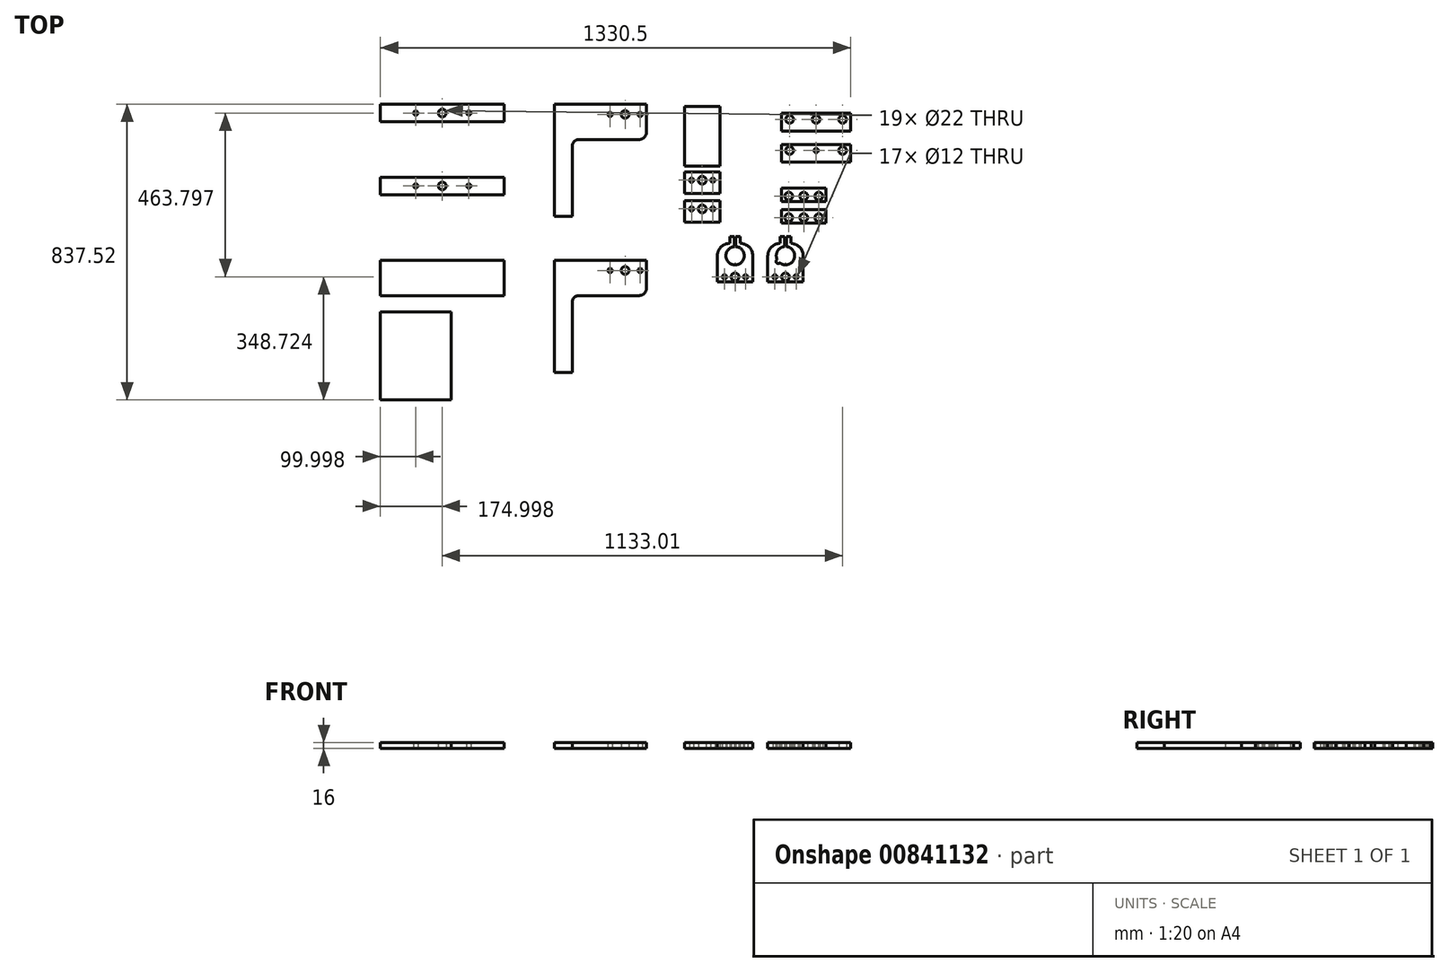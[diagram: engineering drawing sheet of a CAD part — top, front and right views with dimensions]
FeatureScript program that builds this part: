
annotation { "Feature Type Name" : "Feature", "Feature Type Description" : "" }
export const myFeature = defineFeature(function(context is Context, id is Id, definition is map)
    precondition{}
    {
        {
            var Q0;
            Q0=qCreatedBy(makeId("Top.planeOp"),FACE);
            var sketch = newSketch(context, id + "F0", { "sketchPlane" : qUnion([Q0])});
            skLineSegment(sketch, "E0.bottom", {"start": v(-793.1, 335.3) * mm, "end": v(-443.1, 335.3) * mm});
            skLineSegment(sketch, "E0.top", {"start": v(-793.1, 285.3) * mm, "end": v(-443.1, 285.3) * mm});
            skLineSegment(sketch, "E0.left", {"start": v(-793.1, 335.3) * mm, "end": v(-793.1, 285.3) * mm});
            skLineSegment(sketch, "E0.right", {"start": v(-443.1, 335.3) * mm, "end": v(-443.1, 285.3) * mm});
            skLineSegment(sketch, "E1.bottom", {"start": v(-793.1, 100) * mm, "end": v(-443.1, 100) * mm});
            skLineSegment(sketch, "E1.top", {"start": v(-793.1, 0) * mm, "end": v(-443.1, 0) * mm});
            skLineSegment(sketch, "E1.left", {"start": v(-793.1, 100) * mm, "end": v(-793.1, 0) * mm});
            skLineSegment(sketch, "E1.right", {"start": v(-443.1, 100) * mm, "end": v(-443.1, 0) * mm});
            skLineSegment(sketch, "E2", {"start": v(-300.58, 541.75) * mm, "end": v(-40.58, 541.75) * mm});
            skLineSegment(sketch, "E3", {"start": v(-40.58, 541.75) * mm, "end": v(-40.58, 461.75) * mm});
            skLineSegment(sketch, "E4", {"start": v(-60.58, 441.75) * mm, "end": v(-230.58, 441.75) * mm});
            skLineSegment(sketch, "E5", {"start": v(-250.58, 421.75) * mm, "end": v(-250.58, 223.75) * mm});
            skLineSegment(sketch, "E6", {"start": v(-250.58, 223.75) * mm, "end": v(-300.58, 223.75) * mm});
            skLineSegment(sketch, "E7", {"start": v(-300.58, 223.75) * mm, "end": v(-300.58, 541.75) * mm});
            skCircle(sketch, "E8", {"center": v(-693.1, 310.3) * mm, "radius": 6 * mm});
            skCircle(sketch, "E9", {"center": v(-543.1, 310.3) * mm, "radius": 6 * mm});
            skLineSegment(sketch, "E10", {"start": v(-793.1, 310.3) * mm, "end": v(-443.1, 310.3) * mm, "construction": true});
            skCircle(sketch, "E11", {"center": v(-618.1, 310.3) * mm, "radius": 11 * mm});
            skLineSegment(sketch, "E12.bottom", {"start": v(-793.1, 541.75) * mm, "end": v(-443.1, 541.75) * mm});
            skLineSegment(sketch, "E12.top", {"start": v(-793.1, 491.75) * mm, "end": v(-443.1, 491.75) * mm});
            skLineSegment(sketch, "E12.left", {"start": v(-793.1, 541.75) * mm, "end": v(-793.1, 491.75) * mm});
            skLineSegment(sketch, "E12.right", {"start": v(-443.1, 541.75) * mm, "end": v(-443.1, 491.75) * mm});
            skLineSegment(sketch, "E13", {"start": v(-793.1, 516.75) * mm, "end": v(-443.1, 516.75) * mm, "construction": true});
            skCircle(sketch, "E14", {"center": v(-693.1, 516.75) * mm, "radius": 6 * mm});
            skCircle(sketch, "E15", {"center": v(-543.1, 516.75) * mm, "radius": 6 * mm});
            skCircle(sketch, "E16", {"center": v(-618.1, 516.75) * mm, "radius": 11 * mm});
            skLineSegment(sketch, "E17", {"start": v(-300.58, 100) * mm, "end": v(-40.58, 100) * mm});
            skLineSegment(sketch, "E18", {"start": v(-40.58, 100) * mm, "end": v(-40.58, 20) * mm});
            skLineSegment(sketch, "E19", {"start": v(-60.58, 0) * mm, "end": v(-230.58, 0) * mm});
            skLineSegment(sketch, "E20", {"start": v(-250.58, -20) * mm, "end": v(-250.58, -218) * mm});
            skLineSegment(sketch, "E21", {"start": v(-250.58, -218) * mm, "end": v(-300.58, -218) * mm});
            skLineSegment(sketch, "E22", {"start": v(-300.58, -218) * mm, "end": v(-300.58, 100) * mm});
            skLineSegment(sketch, "E23", {"start": v(-40.58, 512.75) * mm, "end": v(-300.58, 512.75) * mm, "construction": true});
            skLineSegment(sketch, "E24", {"start": v(-40.58, 71) * mm, "end": v(-300.58, 71) * mm, "construction": true});
            skCircle(sketch, "E25", {"center": v(-58.15, 512.75) * mm, "radius": 6 * mm});
            skCircle(sketch, "E26", {"center": v(-143.15, 512.75) * mm, "radius": 6 * mm});
            skCircle(sketch, "E27", {"center": v(-58.15, 71) * mm, "radius": 6 * mm});
            skCircle(sketch, "E28", {"center": v(-143.15, 71) * mm, "radius": 6 * mm});
            skCircle(sketch, "E29", {"center": v(-100.58, 512.75) * mm, "radius": 11 * mm});
            skCircle(sketch, "E30", {"center": v(-100.58, 71) * mm, "radius": 11 * mm});
            skPoint(sketch, "E31.visualSharp", {"position": v(-40.58, 441.75) * mm});
            skArc(sketch, "E31.filletArc", {"start": v(-60.58, 441.75) * mm, "mid": v(-46.44, 447.6) * mm, "end": v(-40.58, 461.75) * mm});
            skPoint(sketch, "E32.visualSharp", {"position": v(-250.58, 441.75) * mm});
            skArc(sketch, "E32.filletArc", {"start": v(-230.58, 441.75) * mm, "mid": v(-244.73, 435.9) * mm, "end": v(-250.58, 421.75) * mm});
            skPoint(sketch, "E33.visualSharp", {"position": v(-40.58, 0) * mm});
            skArc(sketch, "E33.filletArc", {"start": v(-60.58, 0) * mm, "mid": v(-46.44, 5.86) * mm, "end": v(-40.58, 20) * mm});
            skPoint(sketch, "E34.visualSharp", {"position": v(-250.58, 0) * mm});
            skArc(sketch, "E34.filletArc", {"start": v(-230.58, 0) * mm, "mid": v(-244.73, -5.86) * mm, "end": v(-250.58, -20) * mm});
            skLineSegment(sketch, "E35.bottom", {"start": v(-793.1, -45.77) * mm, "end": v(-593.1, -45.77) * mm});
            skLineSegment(sketch, "E35.top", {"start": v(-793.1, -295.77) * mm, "end": v(-593.1, -295.77) * mm});
            skLineSegment(sketch, "E35.left", {"start": v(-793.1, -45.77) * mm, "end": v(-793.1, -295.77) * mm});
            skLineSegment(sketch, "E35.right", {"start": v(-593.1, -45.77) * mm, "end": v(-593.1, -295.77) * mm});
            skLineSegment(sketch, "E36.bottom", {"start": v(67.56, 535) * mm, "end": v(167.56, 535) * mm});
            skLineSegment(sketch, "E36.top", {"start": v(67.56, 367) * mm, "end": v(167.56, 367) * mm});
            skLineSegment(sketch, "E36.left", {"start": v(67.56, 535) * mm, "end": v(67.56, 367) * mm});
            skLineSegment(sketch, "E36.right", {"start": v(167.56, 535) * mm, "end": v(167.56, 367) * mm});
            skLineSegment(sketch, "E37.bottom", {"start": v(67.56, 349.5) * mm, "end": v(167.56, 349.5) * mm});
            skLineSegment(sketch, "E37.top", {"start": v(67.56, 289.5) * mm, "end": v(167.56, 289.5) * mm});
            skLineSegment(sketch, "E37.left", {"start": v(67.56, 349.5) * mm, "end": v(67.56, 289.5) * mm});
            skLineSegment(sketch, "E37.right", {"start": v(167.56, 349.5) * mm, "end": v(167.56, 289.5) * mm});
            skPoint(sketch, "E38.oppositeSnap0", {"position": v(167.56, 319.5) * mm});
            skLineSegment(sketch, "E39.bottom", {"start": v(342.4, 515.9) * mm, "end": v(537.4, 515.9) * mm});
            skLineSegment(sketch, "E39.top", {"start": v(342.4, 465.9) * mm, "end": v(537.4, 465.9) * mm});
            skLineSegment(sketch, "E39.left", {"start": v(342.4, 515.9) * mm, "end": v(342.4, 465.9) * mm});
            skLineSegment(sketch, "E39.right", {"start": v(537.4, 515.9) * mm, "end": v(537.4, 465.9) * mm});
            skLineSegment(sketch, "E40", {"start": v(67.56, 326.5) * mm, "end": v(167.56, 326.5) * mm, "construction": true});
            skCircle(sketch, "E41", {"center": v(117.56, 326.5) * mm, "radius": 11 * mm});
            skCircle(sketch, "E42", {"center": v(87.56, 326.5) * mm, "radius": 6 * mm});
            skCircle(sketch, "E43", {"center": v(147.56, 326.5) * mm, "radius": 6 * mm});
            skLineSegment(sketch, "E44.bottom", {"start": v(67.56, 268.28) * mm, "end": v(167.56, 268.28) * mm});
            skLineSegment(sketch, "E44.top", {"start": v(67.56, 208.28) * mm, "end": v(167.56, 208.28) * mm});
            skLineSegment(sketch, "E44.left", {"start": v(67.56, 268.28) * mm, "end": v(67.56, 208.28) * mm});
            skLineSegment(sketch, "E44.right", {"start": v(167.56, 268.28) * mm, "end": v(167.56, 208.28) * mm});
            skPoint(sketch, "E45.oppositeSnap0", {"position": v(167.56, 238.28) * mm});
            skLineSegment(sketch, "E46", {"start": v(67.56, 245.28) * mm, "end": v(167.56, 245.28) * mm, "construction": true});
            skCircle(sketch, "E47", {"center": v(117.56, 245.28) * mm, "radius": 11 * mm});
            skCircle(sketch, "E48", {"center": v(87.56, 245.28) * mm, "radius": 6 * mm});
            skCircle(sketch, "E49", {"center": v(147.56, 245.28) * mm, "radius": 6 * mm});
            skLineSegment(sketch, "E50", {"start": v(342.4, 498.9) * mm, "end": v(537.4, 498.9) * mm, "construction": true});
            skCircle(sketch, "E51", {"center": v(364.9, 498.9) * mm, "radius": 11 * mm});
            skCircle(sketch, "E52", {"center": v(514.9, 498.9) * mm, "radius": 11 * mm});
            skCircle(sketch, "E53", {"center": v(439.9, 498.9) * mm, "radius": 11 * mm});
            skLineSegment(sketch, "E54.bottom", {"start": v(342.4, 427.64) * mm, "end": v(537.4, 427.64) * mm});
            skLineSegment(sketch, "E54.top", {"start": v(342.4, 377.64) * mm, "end": v(537.4, 377.64) * mm});
            skLineSegment(sketch, "E54.left", {"start": v(342.4, 427.64) * mm, "end": v(342.4, 377.64) * mm});
            skLineSegment(sketch, "E54.right", {"start": v(537.4, 427.64) * mm, "end": v(537.4, 377.64) * mm});
            skLineSegment(sketch, "E55", {"start": v(342.4, 410.64) * mm, "end": v(537.4, 410.64) * mm, "construction": true});
            skCircle(sketch, "E56", {"center": v(364.9, 410.64) * mm, "radius": 11 * mm});
            skCircle(sketch, "E57", {"center": v(514.9, 410.64) * mm, "radius": 11 * mm});
            skCircle(sketch, "E58", {"center": v(439.9, 410.64) * mm, "radius": 6 * mm});
            skLineSegment(sketch, "E59.bottom", {"start": v(342.4, 304.54) * mm, "end": v(467.4, 304.54) * mm});
            skLineSegment(sketch, "E59.top", {"start": v(342.4, 266.54) * mm, "end": v(467.4, 266.54) * mm});
            skLineSegment(sketch, "E59.left", {"start": v(342.4, 304.54) * mm, "end": v(342.4, 266.54) * mm});
            skLineSegment(sketch, "E59.right", {"start": v(467.4, 304.54) * mm, "end": v(467.4, 266.54) * mm});
            skPoint(sketch, "E60.oppositeSnap0", {"position": v(467.4, 285.54) * mm});
            skLineSegment(sketch, "E61", {"start": v(342.4, 281.54) * mm, "end": v(467.4, 281.54) * mm, "construction": true});
            skCircle(sketch, "E62", {"center": v(404.9, 281.54) * mm, "radius": 11 * mm});
            skCircle(sketch, "E63", {"center": v(362.4, 281.54) * mm, "radius": 11 * mm});
            skCircle(sketch, "E64", {"center": v(447.4, 281.54) * mm, "radius": 11 * mm});
            skLineSegment(sketch, "E65.bottom", {"start": v(342.4, 243.72) * mm, "end": v(467.4, 243.72) * mm});
            skLineSegment(sketch, "E65.top", {"start": v(342.4, 205.72) * mm, "end": v(467.4, 205.72) * mm});
            skLineSegment(sketch, "E65.left", {"start": v(342.4, 243.72) * mm, "end": v(342.4, 205.72) * mm});
            skLineSegment(sketch, "E65.right", {"start": v(467.4, 243.72) * mm, "end": v(467.4, 205.72) * mm});
            skPoint(sketch, "E66.oppositeSnap0", {"position": v(467.4, 224.72) * mm});
            skLineSegment(sketch, "E67", {"start": v(342.4, 220.72) * mm, "end": v(467.4, 220.72) * mm, "construction": true});
            skCircle(sketch, "E68", {"center": v(404.9, 220.72) * mm, "radius": 11 * mm});
            skCircle(sketch, "E69", {"center": v(362.4, 220.72) * mm, "radius": 11 * mm});
            skCircle(sketch, "E70", {"center": v(447.4, 220.72) * mm, "radius": 11 * mm});
            skLineSegment(sketch, "E71.bottom", {"start": v(160.46, 78.95) * mm, "end": v(260.46, 78.95) * mm});
            skLineSegment(sketch, "E71.top", {"start": v(160.46, 38.95) * mm, "end": v(260.46, 38.95) * mm});
            skLineSegment(sketch, "E71.left", {"start": v(160.46, 78.95) * mm, "end": v(160.46, 38.95) * mm});
            skLineSegment(sketch, "E71.right", {"start": v(260.46, 78.95) * mm, "end": v(260.46, 38.95) * mm});
            skPoint(sketch, "E72.oppositeSnap0", {"position": v(260.46, 58.95) * mm});
            skLineSegment(sketch, "E73", {"start": v(160.46, 52.95) * mm, "end": v(260.46, 52.95) * mm, "construction": true});
            skCircle(sketch, "E74", {"center": v(210.46, 52.95) * mm, "radius": 11 * mm});
            skCircle(sketch, "E75", {"center": v(180.46, 52.95) * mm, "radius": 6 * mm});
            skCircle(sketch, "E76", {"center": v(240.46, 52.95) * mm, "radius": 6 * mm});
            skCircle(sketch, "E77", {"center": v(210.46, 112.78) * mm, "radius": 26 * mm});
            skPoint(sketch, "E77.centerSnap0", {"position": v(210.46, 78.95) * mm});
            skLineSegment(sketch, "E78.left", {"start": v(160.46, 78.95) * mm, "end": v(160.46, 112.63) * mm});
            skLineSegment(sketch, "E78.right", {"start": v(260.46, 78.95) * mm, "end": v(260.46, 112.63) * mm});
            skPoint(sketch, "E79.visualSharp", {"position": v(160.46, 147.63) * mm});
            skArc(sketch, "E79.filletArc", {"start": v(195.51, 147.63) * mm, "mid": v(170.73, 137.4) * mm, "end": v(160.46, 112.63) * mm});
            skPoint(sketch, "E80.visualSharp", {"position": v(260.46, 147.63) * mm});
            skArc(sketch, "E80.filletArc", {"start": v(260.46, 112.63) * mm, "mid": v(250.21, 137.38) * mm, "end": v(225.46, 147.63) * mm});
            skLineSegment(sketch, "E81.top", {"start": v(195.51, 166.54) * mm, "end": v(225.46, 166.54) * mm});
            skLineSegment(sketch, "E81.left", {"start": v(195.51, 147.63) * mm, "end": v(195.51, 166.54) * mm});
            skLineSegment(sketch, "E81.right", {"start": v(225.46, 147.63) * mm, "end": v(225.46, 166.54) * mm});
            skPoint(sketch, "E82.oppositeSnap0", {"position": v(210.49, 166.54) * mm});
            skLineSegment(sketch, "E83.bottom", {"start": v(208.9, 166.54) * mm, "end": v(212.07, 166.54) * mm});
            skSolve(sketch);
        }
        {
            var Q0;
            Q0 = qSketchRegion(id + "F0", true);
            extrude(context, id + "F1", {"entities" : qUnion([Q0]), "depth" : 16 * mm, "offsetDistance" : 25 * mm});
        }
        {
            var Q0;
            Q0=makeQuery(id+"F1.opExtrude","SWEPT_FACE",FACE,{"disambiguationData":[OSD([sQuery(id+"F0.wireOp",EDGE,"E81.top"),sQuery(id+"F0.wireOp",EDGE,"E83.bottom")])]});
            var sketch = newSketch(context, id + "F2", { "sketchPlane" : qUnion([Q0])});
            skLineSegment(sketch, "E84.bottom", {"start": v(-208.34, 17.1) * mm, "end": v(-212.64, 17.1) * mm});
            skLineSegment(sketch, "E84.top", {"start": v(-208.34, -17.1) * mm, "end": v(-212.64, -17.1) * mm});
            skLineSegment(sketch, "E84.left", {"start": v(-208.34, 17.1) * mm, "end": v(-208.34, -17.1) * mm});
            skLineSegment(sketch, "E84.right", {"start": v(-212.64, 17.1) * mm, "end": v(-212.64, -17.1) * mm});
            skPoint(sketch, "E84.middle", {"position": v(-210.49, 0) * mm});
            skSolve(sketch);
        }
        {
            var Q0;
            Q0 = qSketchRegion(id + "F2", true);
            extrude(context, id + "F3", {"entities" : qUnion([Q0]), "operationType" : NewBodyOperationType.REMOVE, "oppositeDirection" : true, "depth" : 51 * mm, "offsetDistance" : 25 * mm});
        }
        {
            var Q0;
            Q0=makeQuery(id+"F1.opExtrude","SWEPT_BODY",BODY,{"disambiguationData":[OSD([sQuery(id+"F0.wireOp",EDGE,"E71.top"),sQuery(id+"F0.wireOp",EDGE,"E71.left"),sQuery(id+"F0.wireOp",EDGE,"E71.right"),sQuery(id+"F0.wireOp",EDGE,"E74"),sQuery(id+"F0.wireOp",EDGE,"E75"),sQuery(id+"F0.wireOp",EDGE,"E76"),sQuery(id+"F0.wireOp",EDGE,"E77"),sQuery(id+"F0.wireOp",EDGE,"E78.left"),sQuery(id+"F0.wireOp",EDGE,"E78.right"),sQuery(id+"F0.wireOp",EDGE,"E79.filletArc"),sQuery(id+"F0.wireOp",EDGE,"E80.filletArc"),sQuery(id+"F0.wireOp",EDGE,"E81.top"),sQuery(id+"F0.wireOp",EDGE,"E81.left"),sQuery(id+"F0.wireOp",EDGE,"E81.right"),sQuery(id+"F0.wireOp",EDGE,"E83.bottom")])]});
            transform(context, id + "F4", {"entities" : qUnion([Q0]), "transformType" : TransformType.COPY});
        }
        {
            var Q0;
            Q0=makeQuery(id+"F4.opPattern","COPY",BODY,{"derivedFrom":makeQuery(id+"F1.opExtrude","SWEPT_BODY",BODY,{"disambiguationData":[OSD([sQuery(id+"F0.wireOp",EDGE,"E71.top"),sQuery(id+"F0.wireOp",EDGE,"E71.left"),sQuery(id+"F0.wireOp",EDGE,"E71.right"),sQuery(id+"F0.wireOp",EDGE,"E74"),sQuery(id+"F0.wireOp",EDGE,"E75"),sQuery(id+"F0.wireOp",EDGE,"E76"),sQuery(id+"F0.wireOp",EDGE,"E77"),sQuery(id+"F0.wireOp",EDGE,"E78.left"),sQuery(id+"F0.wireOp",EDGE,"E78.right"),sQuery(id+"F0.wireOp",EDGE,"E79.filletArc"),sQuery(id+"F0.wireOp",EDGE,"E80.filletArc"),sQuery(id+"F0.wireOp",EDGE,"E81.top"),sQuery(id+"F0.wireOp",EDGE,"E81.left"),sQuery(id+"F0.wireOp",EDGE,"E81.right"),sQuery(id+"F0.wireOp",EDGE,"E83.bottom")])]}),"instanceName":"1"});
            transform(context, id + "F5", {"entities" : qUnion([Q0]), "transformType" : TransformType.TRANSLATION_3D, "dx" : 142.7 * mm, "dy" : 0 * mm, "dz" : 0 * mm, "makeCopy" : true});
        }
        {
            var Q0;
            Q0=makeQuery(id+"F4.opPattern","COPY",BODY,{"derivedFrom":makeQuery(id+"F1.opExtrude","SWEPT_BODY",BODY,{"disambiguationData":[OSD([sQuery(id+"F0.wireOp",EDGE,"E71.top"),sQuery(id+"F0.wireOp",EDGE,"E71.left"),sQuery(id+"F0.wireOp",EDGE,"E71.right"),sQuery(id+"F0.wireOp",EDGE,"E74"),sQuery(id+"F0.wireOp",EDGE,"E75"),sQuery(id+"F0.wireOp",EDGE,"E76"),sQuery(id+"F0.wireOp",EDGE,"E77"),sQuery(id+"F0.wireOp",EDGE,"E78.left"),sQuery(id+"F0.wireOp",EDGE,"E78.right"),sQuery(id+"F0.wireOp",EDGE,"E79.filletArc"),sQuery(id+"F0.wireOp",EDGE,"E80.filletArc"),sQuery(id+"F0.wireOp",EDGE,"E81.top"),sQuery(id+"F0.wireOp",EDGE,"E81.left"),sQuery(id+"F0.wireOp",EDGE,"E81.right"),sQuery(id+"F0.wireOp",EDGE,"E83.bottom")])]}),"instanceName":"1"});
            deleteBodies(context, id + "F6", {"entities" : qUnion([Q0])});
        }
        {
            var Q0;
            Q0=makeQuery(id+"F5.opPattern","COPY",FACE,{"derivedFrom":makeQuery(id+"F4.opPattern","COPY",FACE,{"derivedFrom":makeQuery(id+"F1.opExtrude","CAP_FACE",FACE,{"disambiguationData":[OSD([sQuery(id+"F0.wireOp",EDGE,"E71.top"),sQuery(id+"F0.wireOp",EDGE,"E71.left"),sQuery(id+"F0.wireOp",EDGE,"E71.right"),sQuery(id+"F0.wireOp",EDGE,"E74"),sQuery(id+"F0.wireOp",EDGE,"E75"),sQuery(id+"F0.wireOp",EDGE,"E76"),sQuery(id+"F0.wireOp",EDGE,"E77"),sQuery(id+"F0.wireOp",EDGE,"E78.left"),sQuery(id+"F0.wireOp",EDGE,"E78.right"),sQuery(id+"F0.wireOp",EDGE,"E79.filletArc"),sQuery(id+"F0.wireOp",EDGE,"E80.filletArc"),sQuery(id+"F0.wireOp",EDGE,"E81.top"),sQuery(id+"F0.wireOp",EDGE,"E81.left"),sQuery(id+"F0.wireOp",EDGE,"E81.right"),sQuery(id+"F0.wireOp",EDGE,"E83.bottom")])],"isStart":false}),"instanceName":"1"}),"instanceName":"1"});
            var sketch = newSketch(context, id + "F7", { "sketchPlane" : qUnion([Q0])});
            skCircle(sketch, "E85", {"center": v(332.58, 96.9) * mm, "radius": 6.4 * mm});
            skSolve(sketch);
        }
        {
            var Q0;
            Q0 = qSketchRegion(id + "F7", true);
            extrude(context, id + "F8", {"entities" : qUnion([Q0]), "operationType" : NewBodyOperationType.REMOVE, "endBound" : BoundingType.THROUGH_ALL, "oppositeDirection" : true, "depth" : 25 * mm, "offsetDistance" : 25 * mm});
        }
    });
